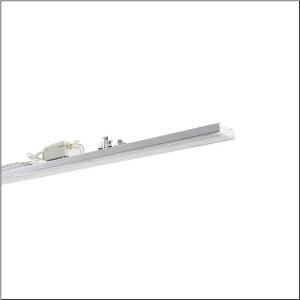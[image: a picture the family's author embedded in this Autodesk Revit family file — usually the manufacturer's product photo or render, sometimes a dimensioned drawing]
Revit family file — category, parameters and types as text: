
# Revit family: licross_21_recessed_ho_52te1edv4lxs
name_source: partatom
category: Lighting Fixtures
units: mm (PartAtom-declared; Revit-internal decimal feet)

## family parameters
Cut with Voids When Loaded = No
Host = Face
Light Source = No
Part Type = Normal
Room Calculation Point = No
Round Connector Dimension = Use Diameter
Shared = No

## types (1)
- --- (1 x LED, 20000 lm, 112.9 W, 4000K)
    Apparent Load = 113 VA
    CIE Flux Codes = 85 95 99 100 100
    Color Rendering = 80
    Color Temperature = 4000K
    Default Elevation = 1800 mm
    Description = Licross 21 Recessed HO, luminaire insert, of sheet steel, galvanised, coil coated, white, length: 2.250mm, width: 66mm, height: 67mm, LED rated luminous flux: 20.000lm, light colour: 840, SDCM (Standard Deviation of Colour Matching)MacAdam ≤ 3 SDCM (initial), control gear: DALI 2, with plug, 5-pole, with phase selection, mains connection: 220..240V, AC, 50/60Hz, rated input power: 113W, internal wiring halogen-free, primary light control with lens, of plastic, primary optical cover: cover, of PMMA, light emission: direct distribution, primary light characteristic: symmetric, protection rating (complete): IP54, insulation class (complete): insulation class I (protective earthing), certification: CE, ENEC, VDE, UKCA, protection symbol: D if used in an environment with non-conductive dust loads with corresponding accessories, impact resistance: IK06, permissible ambient temperature for indoor applications: -40..+35°C, corresponds to IFS (International Featured Standards) requirements for safety and quality in the food industry, reducing of maximum allowable ambient temperature of 5°C with ceiling mounting, LABS conformity tested according to VDMA 24364:2018-05, The light source and the operating device comply with the requirements of the Ecodesign Regulation (EU) 2019/2020 and are replaceable in accordance with this regulation, packaging unit: 1 piece
    Height = 58 mm
    Lamp = 1 x LED
    Lamp Light Flux = 20000 lm
    Lamp Power = 112.9 W
    Lamp count = 1
    Length = 2250 mm
    Luminous efficacy = 177 lm/W
    Manufacturer = Siteco
    ModVariant = No
    Model = 52TE1EDV4LXS
    Mounting Place = Ceiling
    Mounting Type = Pendant
    Number of Poles = 1
    OnlyDefault = Yes
    Power Factor = 1
    Product Name = Licross 21 Recessed HO
    Product group = luminaire insert | ceiling pendant
    ProductGroupID = 901
    Protection Class = Protection class I
    Protection Degree = IP 54
    RLX_Detail_Level = 1
    RLX_Emergency_Light_Flux = 0 lm
    RLX_Emergency_Type = 0
    RLX_Emergency_Type_DB = No
    RlxData = <blob elided: 29789 chars, md5=a61e83f1>
    Socket = socket
    Standby Power = 0 W
    System Light Flux = 20000 lm
    System Power = 113 W
    Type Comments = factory setting: luminous flux: 100 % | dim-lin: 254 | 438 mA
    Type Image = l_1296930.jpg
    URL = http://relux.com
    VarID = @adj_127103
    Voltage = 0 V
    Weight = 0.00 kg
    Width = 66 mm

## geometry (parser evidence)
native form markers: Blend x4, Sweep x11
no freeform markers — native parametric forms only
